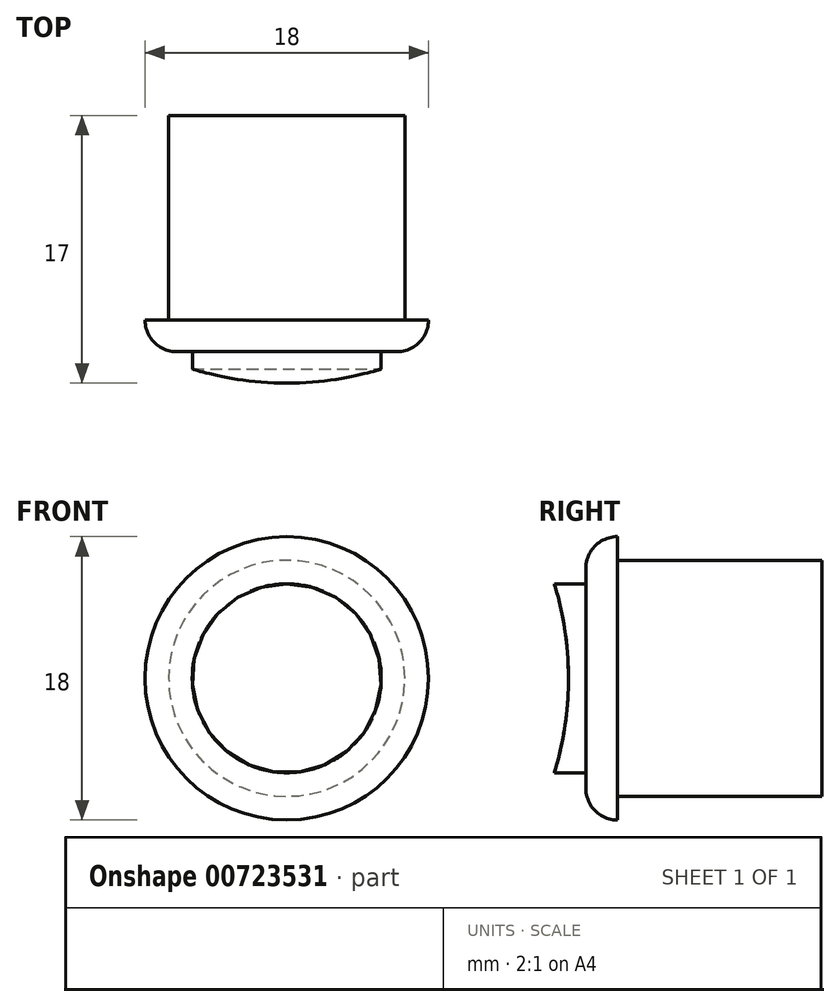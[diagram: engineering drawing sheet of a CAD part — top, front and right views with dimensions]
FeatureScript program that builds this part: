
annotation { "Feature Type Name" : "Feature", "Feature Type Description" : "" }
export const myFeature = defineFeature(function(context is Context, id is Id, definition is map)
    precondition{}
    {
        {
            var Q0;
            Q0=qCreatedBy(makeId("Front.planeOp"),FACE);
            var sketch = newSketch(context, id + "F0", { "sketchPlane" : qUnion([Q0])});
            skCircle(sketch, "E0", {"center": v(0, 0) * mm, "radius": 7.5 * mm});
            skSolve(sketch);
        }
        {
            var Q0;
            Q0 = qSketchRegion(id + "F0", true);
            extrude(context, id + "F1", {"entities" : qUnion([Q0]), "oppositeDirection" : true, "depth" : 15 * mm, "offsetDistance" : 25 * mm});
        }
        {
            var Q0;
            Q0=qCreatedBy(makeId("Front.planeOp"),FACE);
            var sketch = newSketch(context, id + "F2", { "sketchPlane" : qUnion([Q0])});
            skCircle(sketch, "E1", {"center": v(0, 0) * mm, "radius": 9 * mm});
            skSolve(sketch);
        }
        {
            var Q0;
            Q0 = qSketchRegion(id + "F2", true);
            extrude(context, id + "F3", {"entities" : qUnion([Q0]), "operationType" : NewBodyOperationType.ADD, "oppositeDirection" : true, "depth" : 2 * mm, "offsetDistance" : 25 * mm});
        }
        {
            var Q0;
            Q0=qCreatedBy(makeId("Front.planeOp"),FACE);
            var sketch = newSketch(context, id + "F4", { "sketchPlane" : qUnion([Q0])});
            skCircle(sketch, "E2", {"center": v(0, 0) * mm, "radius": 6 * mm});
            skSolve(sketch);
        }
        {
            var Q0;
            Q0 = qSketchRegion(id + "F4", true);
            extrude(context, id + "F5", {"entities" : qUnion([Q0]), "operationType" : NewBodyOperationType.ADD, "depth" : 2 * mm, "offsetDistance" : 25 * mm});
        }
        {
            var Q0;
            Q0=qCreatedBy(makeId("Right.planeOp"),FACE);
            var sketch = newSketch(context, id + "F6", { "sketchPlane" : qUnion([Q0])});
            skLineSegment(sketch, "E3", {"start": v(0, 0) * mm, "end": v(0, 6) * mm, "construction": true});
            skLineSegment(sketch, "E4", {"start": v(0, 6) * mm, "end": v(-2, 6) * mm, "construction": true});
            skLineSegment(sketch, "E5", {"start": v(-2, 6) * mm, "end": v(-2, -6) * mm});
            skLineSegment(sketch, "E6", {"start": v(-2, -6) * mm, "end": v(0, -6) * mm, "construction": true});
            skLineSegment(sketch, "E7", {"start": v(0, -6) * mm, "end": v(0, 0) * mm, "construction": true});
            skArc(sketch, "E8", {"start": v(-2, -6) * mm, "mid": v(-1.11, 0) * mm, "end": v(-2, 6) * mm});
            skSolve(sketch);
        }
        {
            var Q0;
            Q0 = qSketchRegion(id + "F6", true);
            extrude(context, id + "F7", {"entities" : qUnion([Q0]), "operationType" : NewBodyOperationType.REMOVE, "endBound" : BoundingType.SYMMETRIC, "oppositeDirection" : true, "depth" : 25 * mm, "offsetDistance" : 25 * mm});
        }
        {
            var Q0;
            Q0=makeQuery(id+"F3.opExtrude","CAP_EDGE",EDGE,{"disambiguationData":[OSD([sQuery(id+"F2.wireOp",EDGE,"E1")])],"isStart":true});
            fillet(context, id + "F8", {"entities" : qUnion([Q0]), "radius" : 2 * mm, "tangentPropagation" : true, "allowEdgeOverflow" : false});
        }
    });
